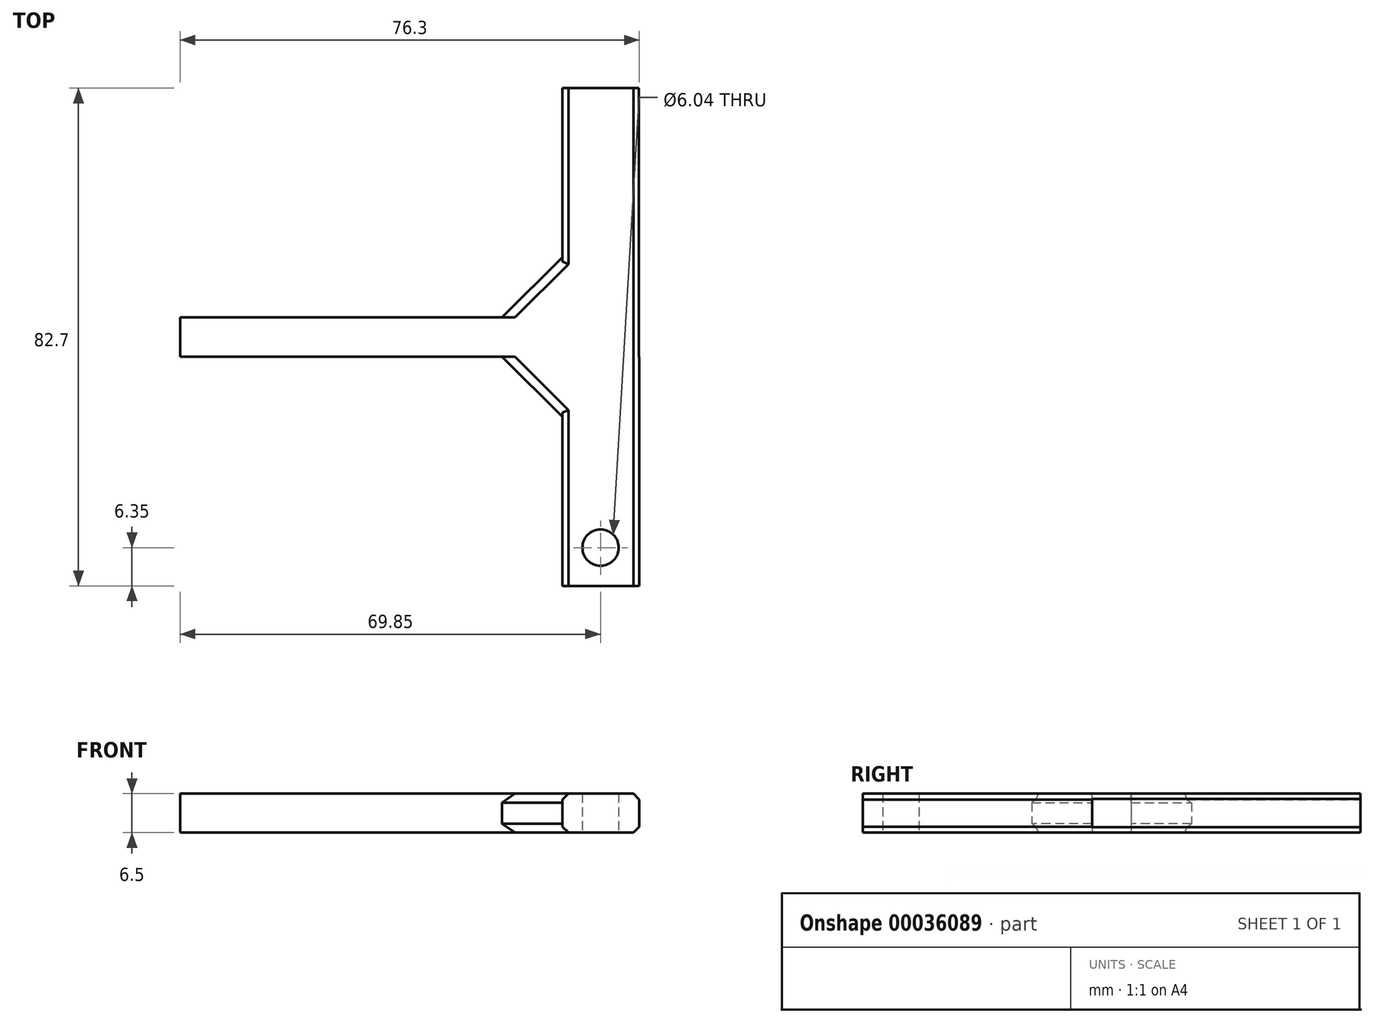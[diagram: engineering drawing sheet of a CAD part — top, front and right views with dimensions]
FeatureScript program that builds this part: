
annotation { "Feature Type Name" : "Feature", "Feature Type Description" : "" }
export const myFeature = defineFeature(function(context is Context, id is Id, definition is map)
    precondition{}
    {
        {
            var Q0;
            Q0=qCreatedBy(makeId("Top.planeOp"),FACE);
            var sketch = newSketch(context, id + "F0", { "sketchPlane" : qUnion([Q0])});
            skLineSegment(sketch, "E0.rect.bottom", {"start": v(38.1, 3.25) * mm, "end": v(-38.1, 3.25) * mm});
            skLineSegment(sketch, "E0.rect.top", {"start": v(38.1, -3.25) * mm, "end": v(-38.1, -3.25) * mm});
            skLineSegment(sketch, "E0.rect.left", {"start": v(38.1, 3.25) * mm, "end": v(38.1, -3.25) * mm});
            skLineSegment(sketch, "E0.rect.right", {"start": v(-38.1, 3.25) * mm, "end": v(-38.1, -3.25) * mm});
            skPoint(sketch, "E0.rect.middle", {"position": v(0, 0) * mm});
            skLineSegment(sketch, "E1.bottom", {"start": v(38.1, 3.25) * mm, "end": v(25.4, 3.25) * mm});
            skLineSegment(sketch, "E1.top", {"start": v(38.1, 41.35) * mm, "end": v(25.4, 41.35) * mm});
            skLineSegment(sketch, "E1.left", {"start": v(38.1, 3.25) * mm, "end": v(38.1, 41.35) * mm});
            skLineSegment(sketch, "E1.right", {"start": v(25.4, 3.25) * mm, "end": v(25.4, 41.35) * mm});
            skLineSegment(sketch, "E2.bottom", {"start": v(25.4, -3.25) * mm, "end": v(38.2, -3.25) * mm});
            skLineSegment(sketch, "E2.top", {"start": v(25.4, -41.35) * mm, "end": v(38.2, -41.35) * mm});
            skLineSegment(sketch, "E2.left", {"start": v(25.4, -3.25) * mm, "end": v(25.4, -41.35) * mm});
            skLineSegment(sketch, "E2.right", {"start": v(38.2, -3.25) * mm, "end": v(38.2, -41.35) * mm});
            skLineSegment(sketch, "E3", {"start": v(15.4, 3.25) * mm, "end": v(25.4, 13.25) * mm});
            skLineSegment(sketch, "E4", {"start": v(15.4, -3.25) * mm, "end": v(25.4, -13.25) * mm});
            skCircle(sketch, "E5", {"center": v(31.75, -35) * mm, "radius": 3.02 * mm});
            skSolve(sketch);
        }
        {
            var Q0;
            Q0 = qSketchRegion(id + "F0", true);
            extrude(context, id + "F1", {"entities" : qUnion([Q0]), "depth" : 6.5 * mm});
        }
        {
            var Q0;
            Q0=makeQuery(id+"F1.opExtrude","CAP_EDGE",EDGE,{"disambiguationData":[OSD([sQuery(id+"F0.wireOp",EDGE,"E4")])],"isStart":false});
            var Q1;
            Q1=makeQuery(id+"F1.opExtrude","CAP_EDGE",EDGE,{"disambiguationData":[OSD([sQuery(id+"F0.wireOp",EDGE,"E3")])],"isStart":false});
            var Q2;
            Q2=makeQuery(id+"F1.opExtrude","CAP_EDGE",EDGE,{"disambiguationData":[OSD([sQuery(id+"F0.wireOp",EDGE,"E3")])],"isStart":true});
            var Q3;
            Q3=makeQuery(id+"F1.opExtrude","CAP_EDGE",EDGE,{"disambiguationData":[OSD([sQuery(id+"F0.wireOp",EDGE,"E4")])],"isStart":true});
            chamfer(context, id + "F2", {"entities" : qUnion([Q0, Q1, Q2, Q3]), "width" : 1.5 * mm, "tangentPropagation" : true});
        }
        {
            var Q0;
            Q0=makeQuery(id+"F1.opExtrude","CAP_EDGE",EDGE,{"disambiguationData":[OSD([sQuery(id+"F0.wireOp",EDGE,"E2.left")])],"isStart":false});
            var Q1;
            Q1=makeQuery(id+"F1.opExtrude","CAP_EDGE",EDGE,{"disambiguationData":[OSD([sQuery(id+"F0.wireOp",EDGE,"E2.left")])],"isStart":true});
            var Q2;
            Q2=makeQuery(id+"F1.opExtrude","CAP_EDGE",EDGE,{"disambiguationData":[OSD([sQuery(id+"F0.wireOp",EDGE,"E1.right")])],"isStart":false});
            var Q3;
            Q3=makeQuery(id+"F1.opExtrude","CAP_EDGE",EDGE,{"disambiguationData":[OSD([sQuery(id+"F0.wireOp",EDGE,"E1.right")])],"isStart":true});
            var Q4;
            Q4=makeQuery(id+"F1.opExtrude","CAP_EDGE",EDGE,{"disambiguationData":[OSD([sQuery(id+"F0.wireOp",EDGE,"E2.right")])],"isStart":false});
            var Q5;
            Q5=makeQuery(id+"F1.opExtrude","CAP_EDGE",EDGE,{"disambiguationData":[OSD([sQuery(id+"F0.wireOp",EDGE,"E2.right")])],"isStart":true});
            chamfer(context, id + "F3", {"entities" : qUnion([Q0, Q1, Q2, Q3, Q4, Q5]), "width" : 1 * mm, "tangentPropagation" : true});
        }
    });
